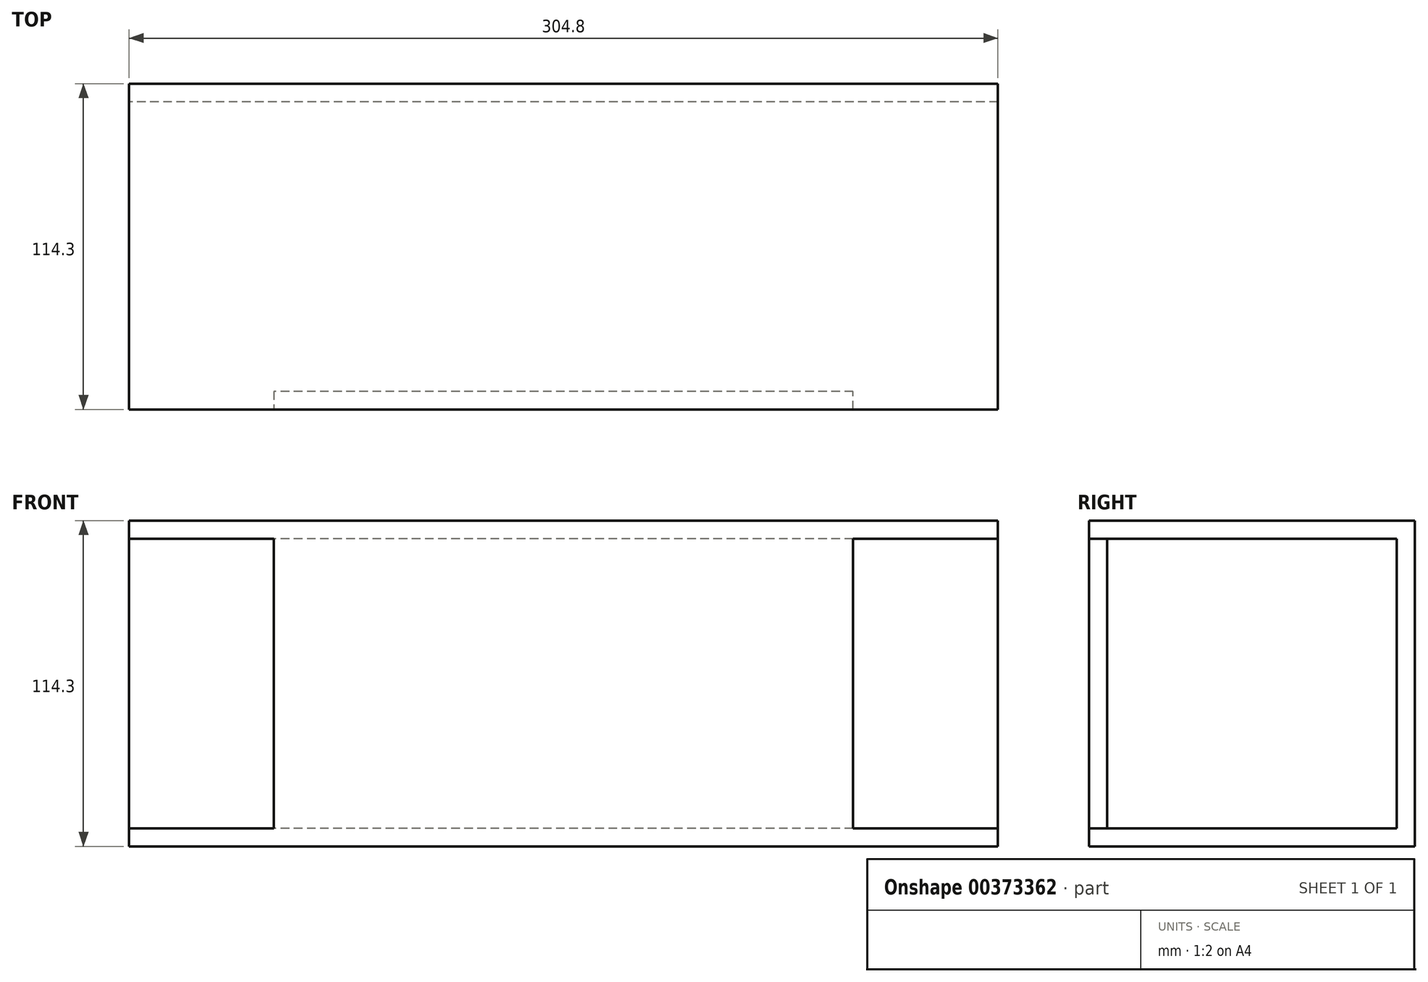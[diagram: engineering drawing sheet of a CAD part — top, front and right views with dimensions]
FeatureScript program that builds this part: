
annotation { "Feature Type Name" : "Feature", "Feature Type Description" : "" }
export const myFeature = defineFeature(function(context is Context, id is Id, definition is map)
    precondition{}
    {
        {
            var Q0;
            Q0=qCreatedBy(makeId("Top.planeOp"),FACE);
            var sketch = newSketch(context, id + "F0", { "sketchPlane" : qUnion([Q0])});
            skLineSegment(sketch, "E0.bottom", {"start": v(-101.6, 57.15) * mm, "end": v(101.6, 57.15) * mm});
            skLineSegment(sketch, "E0.top", {"start": v(-101.6, -57.15) * mm, "end": v(101.6, -57.15) * mm});
            skLineSegment(sketch, "E0.left", {"start": v(-101.6, 57.15) * mm, "end": v(-101.6, -57.15) * mm});
            skLineSegment(sketch, "E0.right", {"start": v(101.6, 57.15) * mm, "end": v(101.6, -57.15) * mm});
            skPoint(sketch, "E0.middle", {"position": v(0, 0) * mm});
            skSolve(sketch);
        }
        {
            var Q0;
            Q0 = qSketchRegion(id + "F0", true);
            extrude(context, id + "F1", {"entities" : qUnion([Q0]), "depth" : 114.3 * mm});
        }
        {
            var Q0;
            Q0=makeQuery(id+"F1.opExtrude","SWEPT_FACE",FACE,{"disambiguationData":[OSD([sQuery(id+"F0.wireOp",EDGE,"E0.left")])]});
            var sketch = newSketch(context, id + "F2", { "sketchPlane" : qUnion([Q0])});
            skLineSegment(sketch, "E1.bottom", {"start": v(-50.8, 107.95) * mm, "end": v(50.8, 107.95) * mm});
            skLineSegment(sketch, "E1.top", {"start": v(-50.8, 6.35) * mm, "end": v(50.8, 6.35) * mm});
            skLineSegment(sketch, "E1.left", {"start": v(-50.8, 107.95) * mm, "end": v(-50.8, 6.35) * mm});
            skLineSegment(sketch, "E1.right", {"start": v(50.8, 107.95) * mm, "end": v(50.8, 6.35) * mm});
            skPoint(sketch, "E1.middle", {"position": v(0, 57.15) * mm});
            skSolve(sketch);
        }
        {
            var Q0;
            Q0 = qSketchRegion(id + "F2", true);
            extrude(context, id + "F3", {"entities" : qUnion([Q0]), "operationType" : NewBodyOperationType.REMOVE, "endBound" : BoundingType.THROUGH_ALL, "oppositeDirection" : true, "depth" : 25.4 * mm});
        }
        {
            var Q0;
            Q0=makeQuery(id+"F1.opExtrude","SWEPT_FACE",FACE,{"disambiguationData":[OSD([sQuery(id+"F0.wireOp",EDGE,"E0.right")])]});
            var sketch = newSketch(context, id + "F4", { "sketchPlane" : qUnion([Q0])});
            skLineSegment(sketch, "E2.bottom", {"start": v(57.15, 114.3) * mm, "end": v(50.8, 114.3) * mm});
            skLineSegment(sketch, "E2.top", {"start": v(57.15, 0) * mm, "end": v(50.8, 0) * mm});
            skLineSegment(sketch, "E2.left", {"start": v(57.15, 114.3) * mm, "end": v(57.15, 0) * mm});
            skLineSegment(sketch, "E2.right", {"start": v(50.8, 114.3) * mm, "end": v(50.8, 0) * mm});
            skLineSegment(sketch, "E3.bottom", {"start": v(-57.15, 0) * mm, "end": v(50.8, 0) * mm});
            skLineSegment(sketch, "E3.top", {"start": v(-57.15, 6.35) * mm, "end": v(50.8, 6.35) * mm});
            skLineSegment(sketch, "E3.left", {"start": v(-57.15, 0) * mm, "end": v(-57.15, 6.35) * mm});
            skLineSegment(sketch, "E3.right", {"start": v(50.8, 0) * mm, "end": v(50.8, 6.35) * mm});
            skLineSegment(sketch, "E4.bottom", {"start": v(-57.15, 114.3) * mm, "end": v(50.8, 114.3) * mm});
            skLineSegment(sketch, "E4.top", {"start": v(-57.15, 107.95) * mm, "end": v(50.8, 107.95) * mm});
            skLineSegment(sketch, "E4.left", {"start": v(-57.15, 114.3) * mm, "end": v(-57.15, 107.95) * mm});
            skLineSegment(sketch, "E4.right", {"start": v(50.8, 114.3) * mm, "end": v(50.8, 107.95) * mm});
            skSolve(sketch);
        }
        {
            var Q0;
            Q0 = qSketchRegion(id + "F4", true);
            extrude(context, id + "F5", {"entities" : qUnion([Q0]), "operationType" : NewBodyOperationType.ADD, "depth" : 50.8 * mm});
        }
        {
            var Q0;
            Q0=makeQuery(id+"F1.opExtrude","SWEPT_FACE",FACE,{"disambiguationData":[OSD([sQuery(id+"F0.wireOp",EDGE,"E0.left")])]});
            var sketch = newSketch(context, id + "F6", { "sketchPlane" : qUnion([Q0])});
            skLineSegment(sketch, "E5.bottom", {"start": v(-57.15, 114.3) * mm, "end": v(-50.8, 114.3) * mm});
            skLineSegment(sketch, "E5.top", {"start": v(-57.15, 0) * mm, "end": v(-50.8, 0) * mm});
            skLineSegment(sketch, "E5.left", {"start": v(-57.15, 114.3) * mm, "end": v(-57.15, 0) * mm});
            skLineSegment(sketch, "E5.right", {"start": v(-50.8, 114.3) * mm, "end": v(-50.8, 0) * mm});
            skLineSegment(sketch, "E6.bottom", {"start": v(-50.8, 0) * mm, "end": v(57.15, 0) * mm});
            skLineSegment(sketch, "E6.top", {"start": v(-50.8, 6.35) * mm, "end": v(57.15, 6.35) * mm});
            skLineSegment(sketch, "E6.left", {"start": v(-50.8, 0) * mm, "end": v(-50.8, 6.35) * mm});
            skLineSegment(sketch, "E6.right", {"start": v(57.15, 0) * mm, "end": v(57.15, 6.35) * mm});
            skLineSegment(sketch, "E7.bottom", {"start": v(-50.8, 114.3) * mm, "end": v(57.15, 114.3) * mm});
            skLineSegment(sketch, "E7.top", {"start": v(-50.8, 107.95) * mm, "end": v(57.15, 107.95) * mm});
            skLineSegment(sketch, "E7.left", {"start": v(-50.8, 114.3) * mm, "end": v(-50.8, 107.95) * mm});
            skLineSegment(sketch, "E7.right", {"start": v(57.15, 114.3) * mm, "end": v(57.15, 107.95) * mm});
            skSolve(sketch);
        }
        {
            var Q0;
            Q0 = qSketchRegion(id + "F6", true);
            extrude(context, id + "F7", {"entities" : qUnion([Q0]), "operationType" : NewBodyOperationType.ADD, "depth" : 50.8 * mm});
        }
    });
